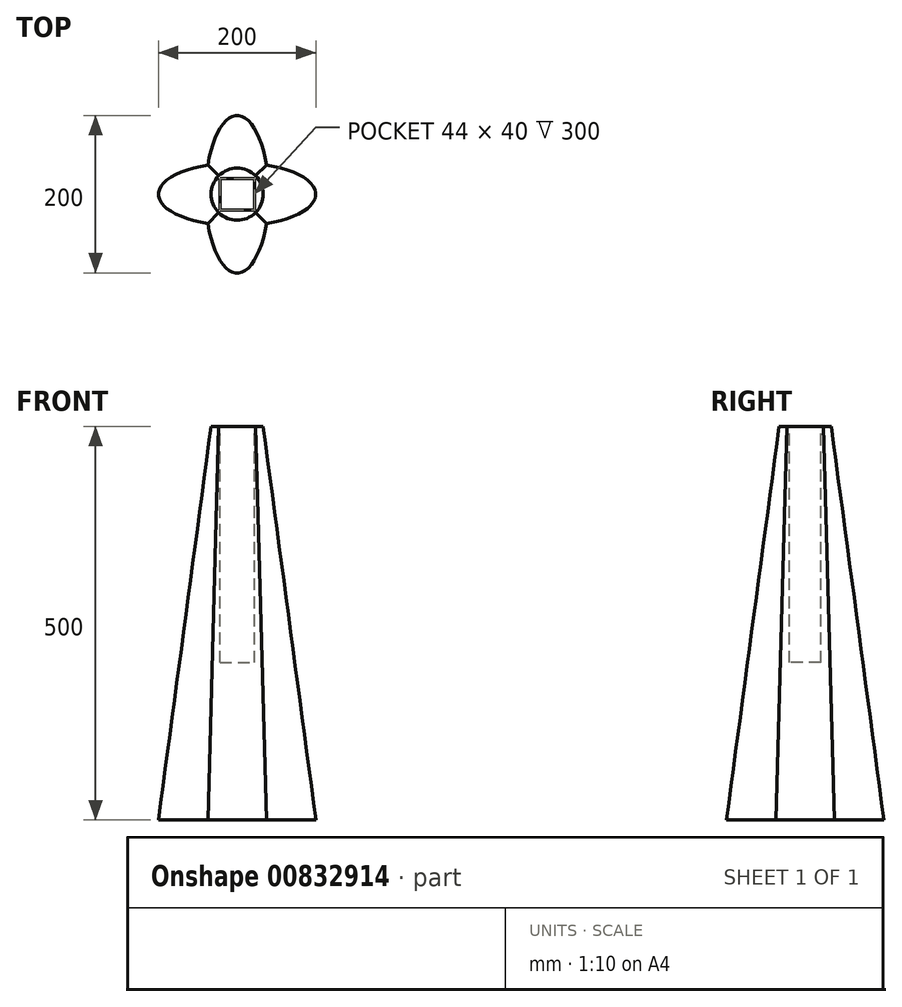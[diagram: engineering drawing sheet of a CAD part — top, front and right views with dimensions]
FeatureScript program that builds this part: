
annotation { "Feature Type Name" : "Feature", "Feature Type Description" : "" }
export const myFeature = defineFeature(function(context is Context, id is Id, definition is map)
    precondition{}
    {
        {
            var Q0;
            Q0=qCreatedBy(makeId("Top.planeOp"),FACE);
            var sketch = newSketch(context, id + "F0", { "sketchPlane" : qUnion([Q0])});
            skEllipticalArc(sketch, "E0", {});
            skEllipticalArc(sketch, "E1", {});
            skEllipticalArc(sketch, "E2.trimOffspring", {});
            skEllipticalArc(sketch, "E3.trimOffspring", {});
            const initialGuessF0  = {"E0": [0, 0, 1, 0, 0.1, 0.04, 1.9513027039072612, 4.331882603272325], "E1": [0, 0, 0, -1, 0.1, 0.04, 5.092895357497055, 1.1902899496825317], "E2.trimOffspring": [0, 0, 1, 0, 0.1, 0.04, 5.092895357497055, 1.1902899496825319], "E3.trimOffspring": [0, 0, 0, -1, 0.1, 0.04, 1.9513027039072615, 4.331882603272325]};
            skSetInitialGuess(sketch, initialGuessF0);
            skSolve(sketch);
        }
        {
            var Q0;
            Q0=qCreatedBy(makeId("Top.planeOp"),FACE);
            cPlane(context, id + "F1", {"entities" : qUnion([Q0]), "cplaneType" : CPlaneType.OFFSET, "offset" : 500 * mm, "width" : 150 * mm, "height" : 150 * mm});
        }
        {
            var Q0;
            Q0=qCreatedBy(id+"F1.planeOp",FACE);
            var sketch = newSketch(context, id + "F2", { "sketchPlane" : qUnion([Q0])});
            skCircle(sketch, "E4", {"center": v(0, 0) * mm, "radius": 33.08 * mm});
            skSolve(sketch);
        }
        {
            var Q0;
            Q0=makeQuery(id+"F0.imprint","IMPRINT",FACE,{"disambiguationData":[TD([[makeQuery(id+"F0.imprint","IMPRINT",EDGE,{"derivedFrom":sQuery(id+"F0.wireOp",EDGE,"E0")}),1.0]])]});
            var Q1;
            Q1=makeQuery(id+"F2.imprint","IMPRINT",FACE,{"disambiguationData":[TD([[makeQuery(id+"F2.imprint","IMPRINT",EDGE,{"derivedFrom":sQuery(id+"F2.wireOp",EDGE,"E4")}),1.0]])]});
            loft(context, id + "F3", {"sheetProfilesArray" : [{ "sheetProfileEntities" : qUnion([Q0]) }, { "sheetProfileEntities" : qUnion([Q1]) }]});
        }
        {
            var Q0;
            Q0=qCreatedBy(id+"F1.planeOp",FACE);
            var sketch = newSketch(context, id + "F4", { "sketchPlane" : qUnion([Q0])});
            skLineSegment(sketch, "E5.bottom", {"start": v(-22, 20) * mm, "end": v(22, 20) * mm});
            skLineSegment(sketch, "E5.top", {"start": v(-22, -20) * mm, "end": v(22, -20) * mm});
            skLineSegment(sketch, "E5.left", {"start": v(-22, 20) * mm, "end": v(-22, -20) * mm});
            skLineSegment(sketch, "E5.right", {"start": v(22, 20) * mm, "end": v(22, -20) * mm});
            skSolve(sketch);
        }
        {
            var Q0;
            Q0=makeQuery(id+"F4.imprint","IMPRINT",FACE,{"disambiguationData":[TD([[makeQuery(id+"F4.imprint","IMPRINT",EDGE,{"derivedFrom":sQuery(id+"F4.wireOp",EDGE,"E5.bottom")}),-1.0]])]});
            extrude(context, id + "F5", {"entities" : qUnion([Q0]), "operationType" : NewBodyOperationType.REMOVE, "oppositeDirection" : true, "depth" : 300 * mm, "offsetDistance" : 25 * mm});
        }
    });
